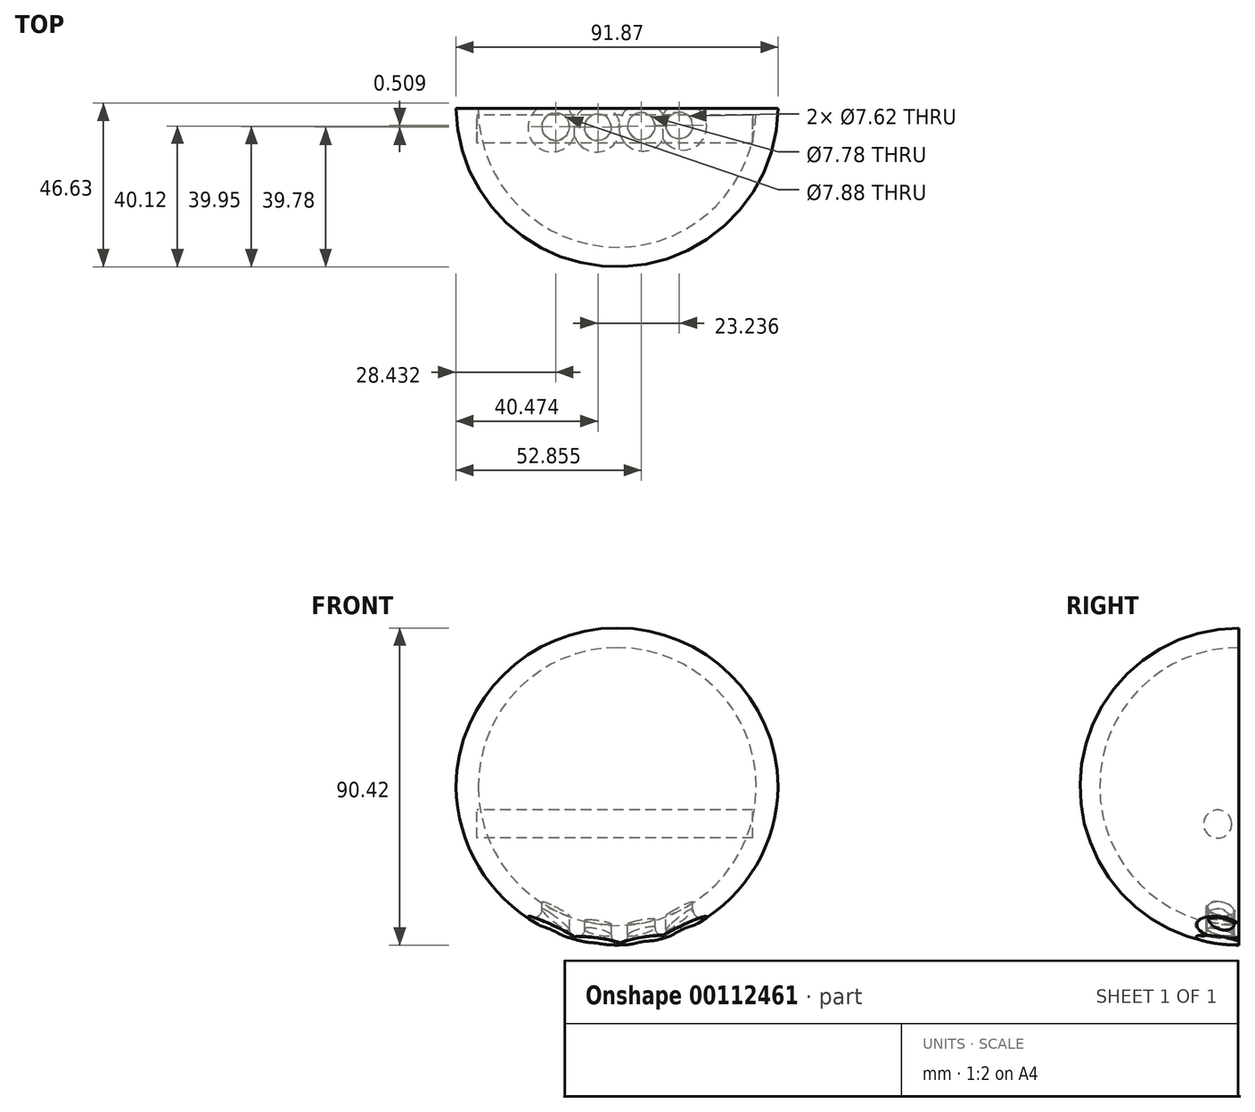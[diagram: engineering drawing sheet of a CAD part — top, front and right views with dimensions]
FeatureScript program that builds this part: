
annotation { "Feature Type Name" : "Feature", "Feature Type Description" : "" }
export const myFeature = defineFeature(function(context is Context, id is Id, definition is map)
    precondition{}
    {
        {
            var Q0;
            Q0=qCreatedBy(makeId("Front.planeOp"),FACE);
            var sketch = newSketch(context, id + "F0", { "sketchPlane" : qUnion([Q0])});
            skCircle(sketch, "E0", {"center": v(0, 0) * mm, "radius": 39.62 * mm});
            skLineSegment(sketch, "E1", {"start": v(0, 0) * mm, "end": v(-46, 0) * mm});
            skLineSegment(sketch, "E2", {"start": v(0, 0) * mm, "end": v(45.87, 0) * mm});
            skArc(sketch, "E3", {"start": v(45.87, 0) * mm, "mid": v(-0.07, 45.2) * mm, "end": v(-46, 0) * mm});
            skSolve(sketch);
        }
        {
            var Q0;
            {var subQ5=sQuery(id+"F0.wireOp",EDGE,"E3");Q0=makeQuery(id+"F0.imprint","IMPRINT",FACE,{"disambiguationData":[TD([[makeQuery(id+"F0.imprint","IMPRINT",EDGE,{"derivedFrom":subQ5}),1.0]])]});}
            var Q1;
            Q1=sQuery(id+"F0.wireOp",EDGE,"E2");
            revolve(context, id + "F1", {"entities" : qUnion([Q0]), "axis" : qUnion([Q1]), "revolveType" : RevolveType.ONE_DIRECTION, "angle" : 180 * degree});
        }
        {
            var Q0;
            Q0=qCreatedBy(makeId("Top.planeOp"),FACE);
            var sketch = newSketch(context, id + "F2", { "sketchPlane" : qUnion([Q0])});
            skLineSegment(sketch, "E4", {"start": v(-28.73, 0) * mm, "end": v(0, 0) * mm, "construction": true});
            skLineSegment(sketch, "E5", {"start": v(0, 0) * mm, "end": v(35.2, 0) * mm, "construction": true});
            skCircle(sketch, "E6", {"center": v(-17.57, -5.26) * mm, "radius": 3.94 * mm});
            skCircle(sketch, "E7", {"center": v(-5.53, -5.43) * mm, "radius": 3.81 * mm});
            skCircle(sketch, "E8", {"center": v(6.86, -5.1) * mm, "radius": 3.89 * mm});
            skCircle(sketch, "E9", {"center": v(17.7, -4.92) * mm, "radius": 3.81 * mm});
            skSolve(sketch);
        }
        {
            var Q0;
            Q0 = qSketchRegion(id + "F2", true);
            extrude(context, id + "F3", {"entities" : qUnion([Q0]), "operationType" : NewBodyOperationType.REMOVE, "oppositeDirection" : true, "depth" : 84.88 * mm});
        }
        {
            var Q0;
            Q0=qCreatedBy(makeId("Right.planeOp"),FACE);
            var sketch = newSketch(context, id + "F4", { "sketchPlane" : qUnion([Q0])});
            skCircle(sketch, "E10", {"center": v(-6, -10.7) * mm, "radius": 4 * mm});
            skSolve(sketch);
        }
        {
            var Q0;
            Q0 = qSketchRegion(id + "F4", true);
            extrude(context, id + "F5", {"entities" : qUnion([Q0]), "depth" : 38.64 * mm, "hasSecondDirection" : true, "secondDirectionOppositeDirection" : true, "secondDirectionDepth" : 40.06 * mm});
        }
        {
            var Q0;
            Q0=makeQuery(id+"F3.boolean.opBoolean","INTERSECT",EDGE,{"derivedFrom":[makeQuery(id+"F1.opRevolve","SWEPT_FACE",FACE,{"disambiguationData":[OSD([sQuery(id+"F0.wireOp",EDGE,"E3")])]}),makeQuery(id+"F3.opExtrude","SWEPT_FACE",FACE,{"disambiguationData":[OSD([sQuery(id+"F2.wireOp",EDGE,"E6")])]})]});
            var Q1;
            Q1=makeQuery(id+"F3.boolean.opBoolean","INTERSECT",EDGE,{"derivedFrom":[makeQuery(id+"F1.opRevolve","SWEPT_FACE",FACE,{"disambiguationData":[OSD([sQuery(id+"F0.wireOp",EDGE,"E3")])]}),makeQuery(id+"F3.opExtrude","SWEPT_FACE",FACE,{"disambiguationData":[OSD([sQuery(id+"F2.wireOp",EDGE,"E7")])]})]});
            var Q2;
            Q2=makeQuery(id+"F3.boolean.opBoolean","INTERSECT",EDGE,{"derivedFrom":[makeQuery(id+"F1.opRevolve","SWEPT_FACE",FACE,{"disambiguationData":[OSD([sQuery(id+"F0.wireOp",EDGE,"E3")])]}),makeQuery(id+"F3.opExtrude","SWEPT_FACE",FACE,{"disambiguationData":[OSD([sQuery(id+"F2.wireOp",EDGE,"E8")])]})]});
            var Q3;
            Q3=makeQuery(id+"F3.boolean.opBoolean","INTERSECT",EDGE,{"derivedFrom":[makeQuery(id+"F1.opRevolve","SWEPT_FACE",FACE,{"disambiguationData":[OSD([sQuery(id+"F0.wireOp",EDGE,"E3")])]}),makeQuery(id+"F3.opExtrude","SWEPT_FACE",FACE,{"disambiguationData":[OSD([sQuery(id+"F2.wireOp",EDGE,"E9")])]})]});
            fillet(context, id + "F6", {"entities" : qUnion([Q0, Q1, Q2, Q3]), "radius" : 2.54 * mm, "tangentPropagation" : true, "allowEdgeOverflow" : false});
        }
    });
